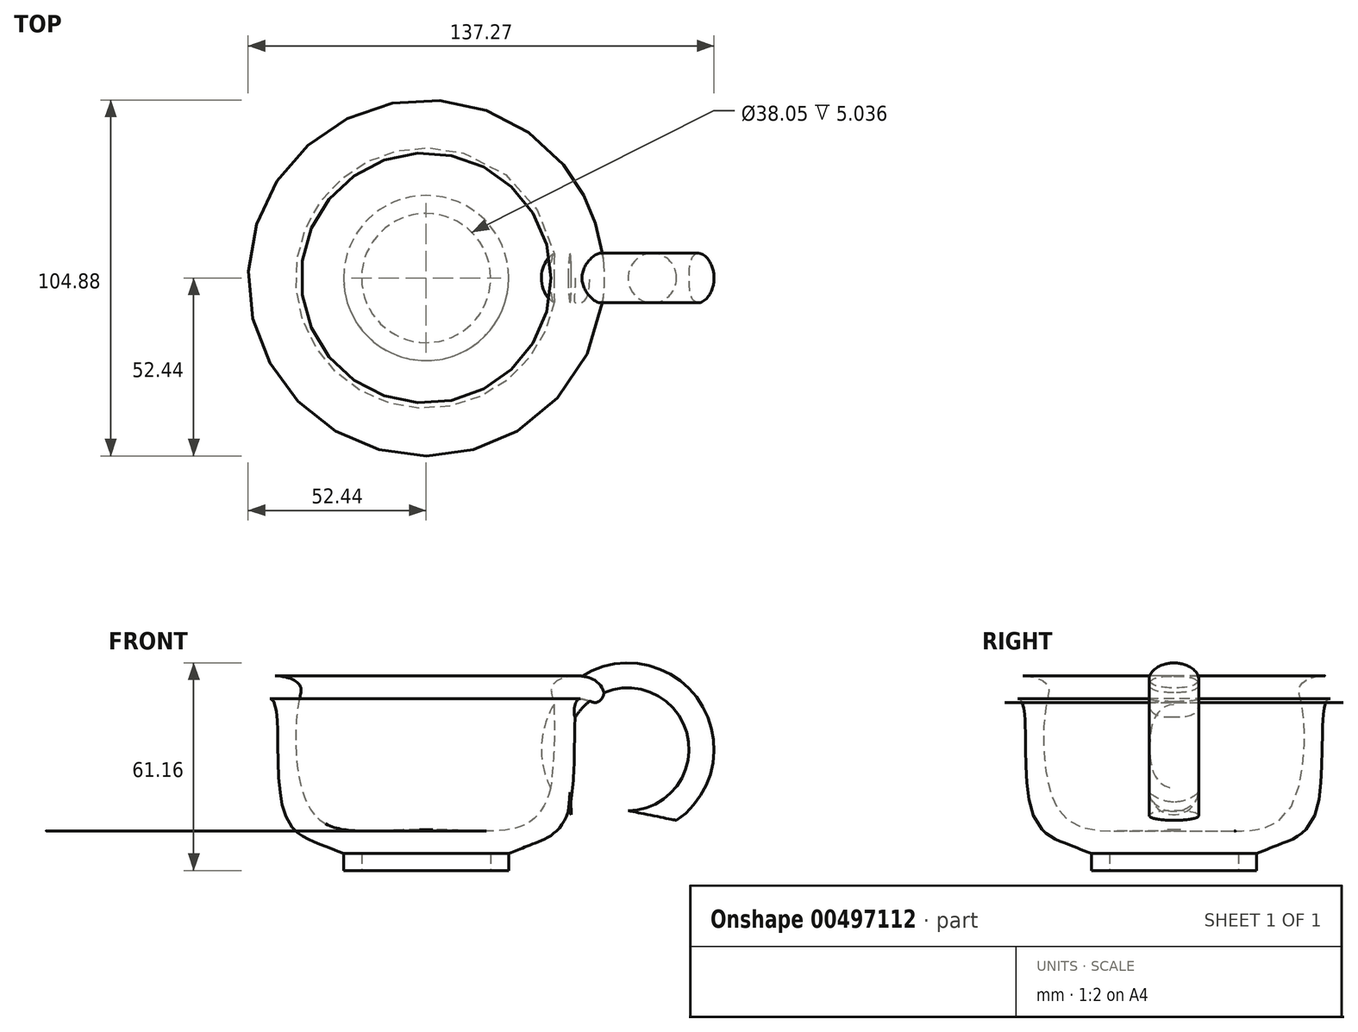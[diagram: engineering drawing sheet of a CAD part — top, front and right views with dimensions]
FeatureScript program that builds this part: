
annotation { "Feature Type Name" : "Feature", "Feature Type Description" : "" }
export const myFeature = defineFeature(function(context is Context, id is Id, definition is map)
    precondition{}
    {
        {
            var Q0;
            Q0=qCreatedBy(makeId("Front.planeOp"),FACE);
            var sketch = newSketch(context, id + "F0", { "sketchPlane" : qUnion([Q0])});
            skLineSegment(sketch, "E0", {"start": v(0, 0) * mm, "end": v(19.02, 0) * mm});
            skLineSegment(sketch, "E1", {"start": v(19.02, 0) * mm, "end": v(19.02, -5.04) * mm});
            skLineSegment(sketch, "E2", {"start": v(19.02, -5.04) * mm, "end": v(24.34, -5.04) * mm});
            skLineSegment(sketch, "E3", {"start": v(24.34, -5.04) * mm, "end": v(24.34, 0) * mm});
            skLineSegment(sketch, "E4", {"start": v(0, 0) * mm, "end": v(0, 48.96) * mm});
            skFitSpline(sketch, "E5", {"points": [v(24.34, 0) * mm, v(30.77, 2.52) * mm, v(41.68, 11.75) * mm, v(45.32, 45.32) * mm, v(50.08, 44.48) * mm, v(52.31, 48.68) * mm, v(44.2, 52.31) * mm, v(37.2, 49.52) * mm, v(37.77, 43.08) * mm, v(33.01, 11.47) * mm, v(0, 7) * mm], "startDerivative": vector(91.88, 29.9) * mm, "endDerivative": vector(-279.32, -4.93) * mm});
            skSolve(sketch);
        }
        {
            var Q0;
            {var subQ1=sQuery(id+"F0.wireOp",EDGE,"E1");Q0=makeQuery(id+"F0.imprint","IMPRINT",FACE,{"disambiguationData":[TD([[makeQuery(id+"F0.imprint","IMPRINT",EDGE,{"derivedFrom":subQ1}),1.0]])]});}
            var Q1;
            Q1=sQuery(id+"F0.wireOp",EDGE,"E4");
            revolve(context, id + "F1", {"entities" : qUnion([Q0]), "axis" : qUnion([Q1]), "revolveType" : RevolveType.FULL});
        }
        {
            var Q0;
            Q0=qCreatedBy(makeId("Right.planeOp"),FACE);
            cPlane(context, id + "F2", {"entities" : qUnion([Q0]), "cplaneType" : CPlaneType.OFFSET, "offset" : 41.68 * mm, "width" : 152.4 * mm, "height" : 152.4 * mm});
        }
        {
            var Q0;
            Q0=qCreatedBy(id+"F2.planeOp",FACE);
            var sketch = newSketch(context, id + "F3", { "sketchPlane" : qUnion([Q0])});
            skCircle(sketch, "E6", {"center": v(0, 19.74) * mm, "radius": 7.3 * mm});
            skSolve(sketch);
        }
        {
            var Q0;
            Q0=qCreatedBy(makeId("Front.planeOp"),FACE);
            var sketch = newSketch(context, id + "F4", { "sketchPlane" : qUnion([Q0])});
            skArc(sketch, "E7", {"start": v(42.41, 16.03) * mm, "mid": v(81.8, 31.94) * mm, "end": v(40.89, 43.37) * mm});
            skSolve(sketch);
        }
        {
            var Q0;
            Q0 = qSketchRegion(id + "F3", true);
            var Q1;
            Q1 = qConstructionFilter(qBodyType(qCreatedBy(id + "F4" ,EDGE), BodyType.WIRE), ConstructionObject.NO);
            sweep(context, id + "F5", {"operationType" : NewBodyOperationType.ADD, "profiles" : qUnion([Q0]), "path" : qUnion([Q1])});
        }
    });
